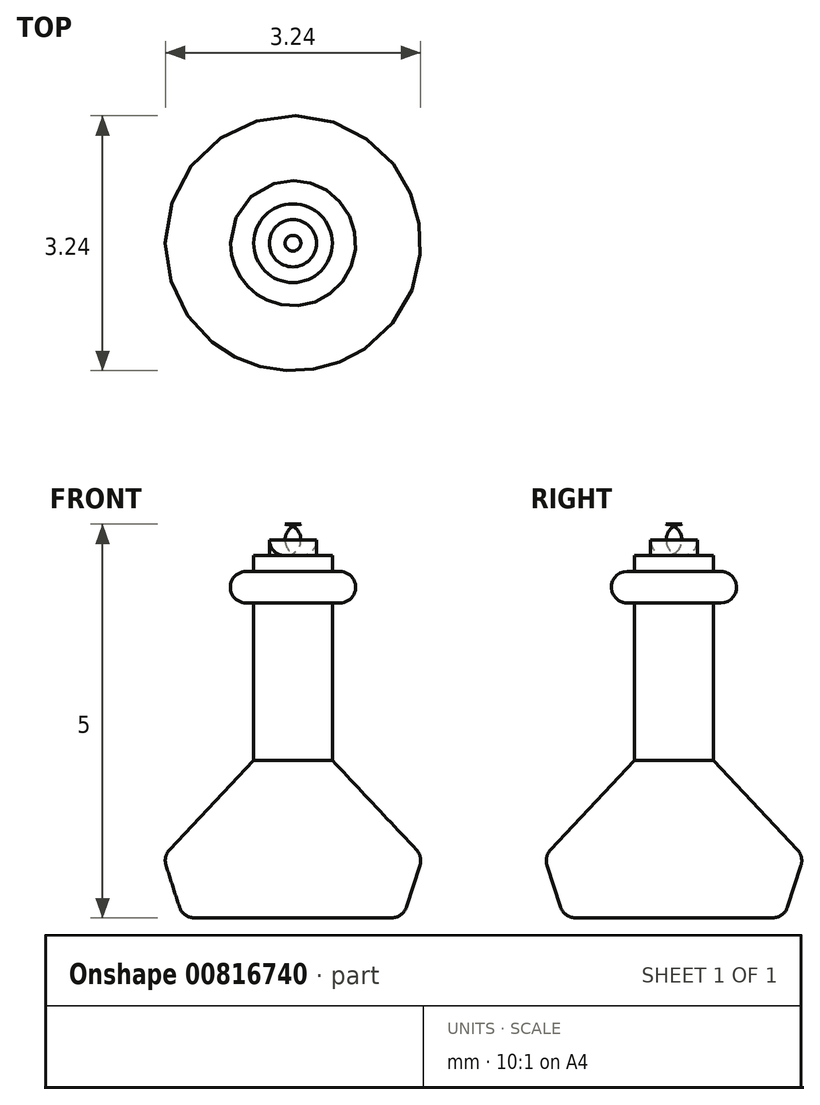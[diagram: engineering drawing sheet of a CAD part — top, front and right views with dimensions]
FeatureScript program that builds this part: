
annotation { "Feature Type Name" : "Feature", "Feature Type Description" : "" }
export const myFeature = defineFeature(function(context is Context, id is Id, definition is map)
    precondition{}
    {
        {
            var Q0;
            Q0=qCreatedBy(makeId("Front.planeOp"),FACE);
            var sketch = newSketch(context, id + "F0", { "sketchPlane" : qUnion([Q0])});
            skLineSegment(sketch, "E0", {"start": v(0, 0) * mm, "end": v(1.4, 0) * mm});
            skLineSegment(sketch, "E1", {"start": v(1.4, 0) * mm, "end": v(1.65, 0.78) * mm});
            skLineSegment(sketch, "E2", {"start": v(1.65, 0.78) * mm, "end": v(0.5, 2) * mm});
            skLineSegment(sketch, "E3", {"start": v(0.5, 2) * mm, "end": v(0.5, 4) * mm});
            skLineSegment(sketch, "E4", {"start": v(0.5, 4) * mm, "end": v(0.8, 4) * mm});
            skLineSegment(sketch, "E5", {"start": v(0.8, 4) * mm, "end": v(0.8, 4.4) * mm});
            skLineSegment(sketch, "E6", {"start": v(0.8, 4.4) * mm, "end": v(0.5, 4.4) * mm});
            skLineSegment(sketch, "E7", {"start": v(0, 5) * mm, "end": v(0, 0) * mm});
            skLineSegment(sketch, "E8", {"start": v(0.5, 4.4) * mm, "end": v(0.5, 4.6) * mm});
            skLineSegment(sketch, "E9", {"start": v(0.5, 4.6) * mm, "end": v(0.3, 4.6) * mm});
            skLineSegment(sketch, "E10", {"start": v(0.3, 4.6) * mm, "end": v(0.3, 5) * mm});
            skLineSegment(sketch, "E11", {"start": v(0.3, 5) * mm, "end": v(0, 5) * mm});
            skSolve(sketch);
        }
        {
            var Q0;
            Q0=makeQuery(id+"F0.imprint","IMPRINT",FACE,{"disambiguationData":[TD([[makeQuery(id+"F0.imprint","IMPRINT",EDGE,{"derivedFrom":sQuery(id+"F0.wireOp",EDGE,"E0")}),1.0]])]});
            var Q1;
            Q1=sQuery(id+"F0.wireOp",EDGE,"E7");
            revolve(context, id + "F1", {"surfaceOperationType" : NewSurfaceOperationType.NEW, "entities" : qUnion([Q0]), "axis" : qUnion([Q1]), "revolveType" : RevolveType.FULL});
        }
        {
            var Q0;
            Q0=makeQuery(id+"F1.opRevolve","SWEPT_EDGE",EDGE,{"disambiguationData":[OSD([sQuery(id+"F0.wireOp",EDGE,"E0"),sQuery(id+"F0.wireOp",EDGE,"E1")])]});
            fillet(context, id + "F2", {"entities" : qUnion([Q0]), "radius" : 0.2 * mm, "tangentPropagation" : true, "allowEdgeOverflow" : false});
        }
        {
            var Q0;
            Q0=makeQuery(id+"F1.opRevolve","SWEPT_EDGE",EDGE,{"disambiguationData":[OSD([sQuery(id+"F0.wireOp",EDGE,"E1"),sQuery(id+"F0.wireOp",EDGE,"E2")])]});
            var Q1;
            Q1=makeQuery(id+"F1.opRevolve","SWEPT_EDGE",EDGE,{"disambiguationData":[OSD([sQuery(id+"F0.wireOp",EDGE,"E10"),sQuery(id+"F0.wireOp",EDGE,"E11")])]});
            fillet(context, id + "F3", {"entities" : qUnion([Q0, Q1]), "radius" : 0.2 * mm, "tangentPropagation" : true, "allowEdgeOverflow" : false});
        }
        {
            var Q0;
            Q0=makeQuery(id+"F1.opRevolve","SWEPT_EDGE",EDGE,{"disambiguationData":[OSD([sQuery(id+"F0.wireOp",EDGE,"E5"),sQuery(id+"F0.wireOp",EDGE,"E6")])]});
            var Q1;
            Q1=makeQuery(id+"F1.opRevolve","SWEPT_EDGE",EDGE,{"disambiguationData":[OSD([sQuery(id+"F0.wireOp",EDGE,"E4"),sQuery(id+"F0.wireOp",EDGE,"E5")])]});
            fillet(context, id + "F4", {"entities" : qUnion([Q0, Q1]), "radius" : 0.2 * mm, "tangentPropagation" : true, "allowEdgeOverflow" : false});
        }
    });
